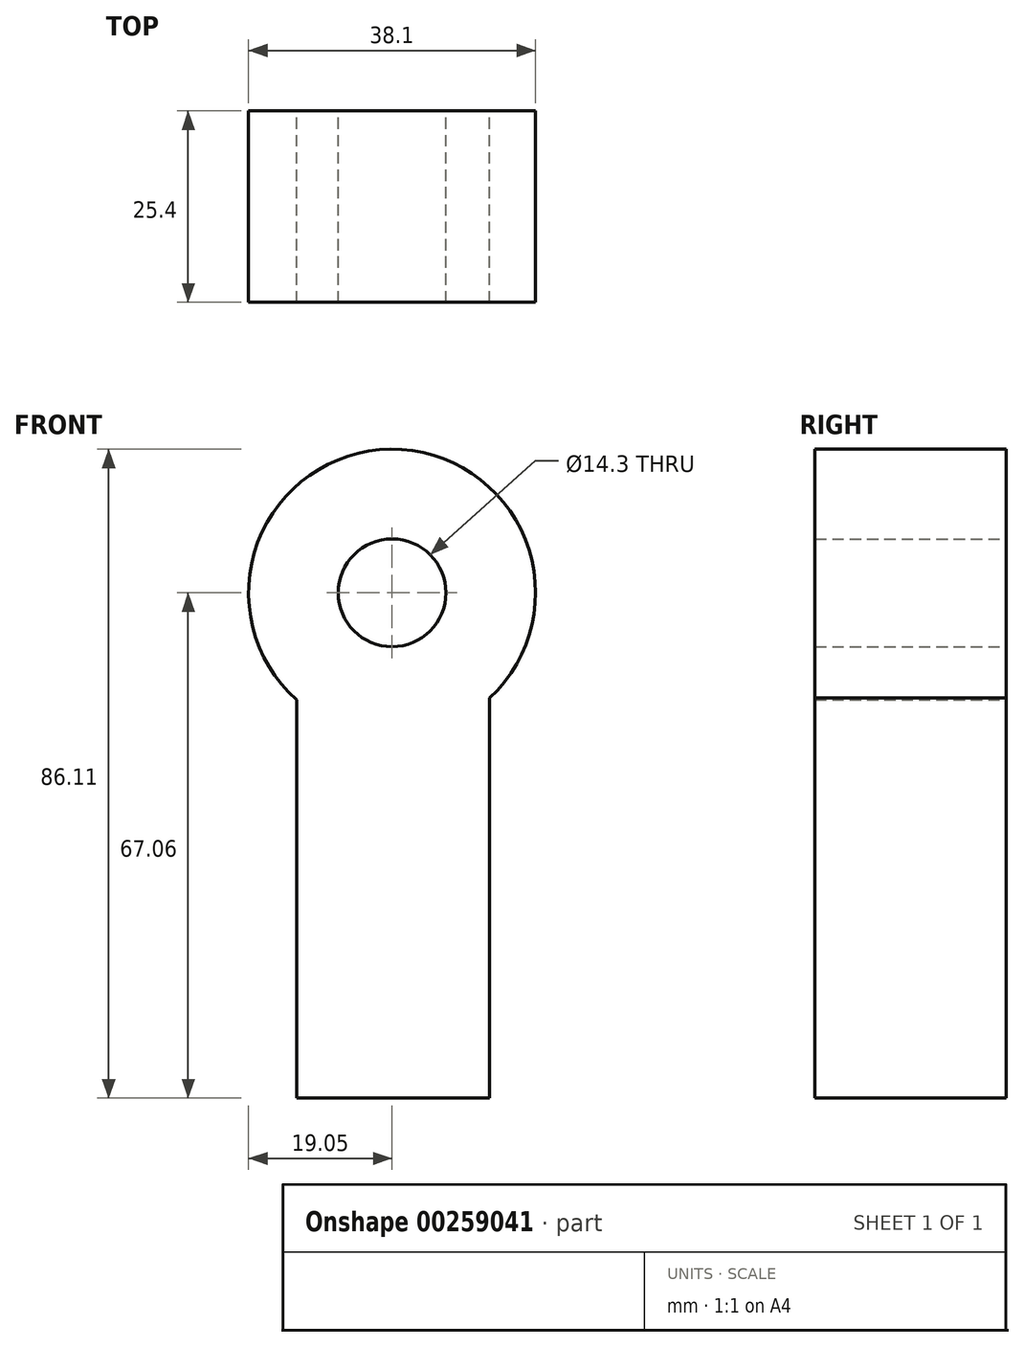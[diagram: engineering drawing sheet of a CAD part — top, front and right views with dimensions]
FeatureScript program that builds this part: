
annotation { "Feature Type Name" : "Feature", "Feature Type Description" : "" }
export const myFeature = defineFeature(function(context is Context, id is Id, definition is map)
    precondition{}
    {
        {
            var Q0;
            Q0=qCreatedBy(makeId("Front.planeOp"),FACE);
            var sketch = newSketch(context, id + "F0", { "sketchPlane" : qUnion([Q0])});
            skCircle(sketch, "E0", {"center": v(0, 0) * mm, "radius": 19.05 * mm});
            skCircle(sketch, "E1", {"center": v(0, 0) * mm, "radius": 7.15 * mm});
            skLineSegment(sketch, "E2", {"start": v(-12.66, -19.05) * mm, "end": v(-12.66, -67.06) * mm});
            skLineSegment(sketch, "E3", {"start": v(-12.66, -67.06) * mm, "end": v(12.95, -67.06) * mm});
            skLineSegment(sketch, "E4", {"start": v(12.95, -67.06) * mm, "end": v(12.95, -13.97) * mm});
            skPoint(sketch, "E5.start.orphan", {"position": v(0, -19.05) * mm});
            skLineSegment(sketch, "E6", {"start": v(-12.66, -19.05) * mm, "end": v(-12.66, -14.23) * mm});
            skSolve(sketch);
        }
        {
            var Q0;
            Q0=makeQuery(id+"F0.imprint","IMPRINT",FACE,{"disambiguationData":[TD([[makeQuery(id+"F0.imprint","IMPRINT",EDGE,{"derivedFrom":sQuery(id+"F0.wireOp",EDGE,"E1")}),-1.0]])]});
            var Q1;
            Q1=makeQuery(id+"F0.imprint","IMPRINT",FACE,{"disambiguationData":[TD([[makeQuery(id+"F0.imprint","IMPRINT",EDGE,{"derivedFrom":sQuery(id+"F0.wireOp",EDGE,"E2")}),1.0]])]});
            extrude(context, id + "F1", {"entities" : qUnion([Q0, Q1]), "depth" : 25.4 * mm});
        }
    });
